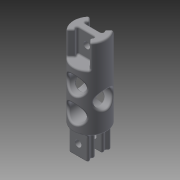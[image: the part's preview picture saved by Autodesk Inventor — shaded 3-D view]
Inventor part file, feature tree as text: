
AUTODESK INVENTOR PART (.ipt)
format: ipt  version: 2013 (Build 170138000, 138)  size: 1,039,872 bytes
history: native  units: mm
features: extrude x6, sketch x3, other x2, fillet x2, folder x1, plane x1
ambient origin geometry x8: Origin, YZ Plane, XZ Plane, XY Plane, X Axis, Y Axis, Z Axis, Center Point
bodies: Solid1 (feature_tree)
feature tree (15):
  folder  "Master Lengths"
  other  "Profile"
  extrude  "Plug Side"  Depth=2.0mm
  extrude  "Fuse Section"  Depth=4.0mm
  plane  "Work Plane2"
  extrude  "Clamp Side Extrude"  TaperAngle=45.0deg  [1 undecoded]
  fillet  "Fillet1"  Radius=15.0mm
  extrude  "Extrusion4"  Depth=35.0mm TaperAngle=0.0deg
  extrude  "Extrusion5"  TaperAngle=0.0deg  [1 undecoded]
  fillet  "Fillet3"  Radius=12.0mm
  extrude  "Extrusion6"  Depth=12.0mm
  other  "Clamp Side"
  sketch  "Sketch4"  dims[d0=4.0mm d2=2.0mm]
  sketch  "Sketch5"  dims[d3=12.7mm d4=4.0mm]
  sketch  "Sketch6"  dims[d5=45.0deg d6=45.0deg d7=15.0mm d8=0.0mm d9=35.0mm d10=0.0mm d11=0.0mm d12=12.0mm d13=12.0mm d14=15.0mm d16=15.0mm d18=50.0mm d19=25.0mm d21=35.0mm d23=-35.0mm d24=15.0mm d25=0.0mm d26=1.0mm d27=1.0mm d28=5.0mm d29=0.0mm d32=40.0mm d33=0.0mm d37=0.0mm d41=10.7mm d42=10.7mm d43=9.883333mm d44=35.0mm d45=9.883333mm d47=10.7mm d49=2.266667mm d50=2.266667mm d51=40.0mm d52=0.0mm d53=1.0mm d54=4.0mm d56=4.0mm d57=7.5mm d58=7.5mm d59=7.5mm d60=7.5mm d61=0.0mm d62=0.0mm d63=20.0mm d64=0.0mm]
note: 2 required parameter values undecoded (feature->parameter linkage not recoverable at this tier; creation-order binding heuristic only, values carry confidence <= 0.55)
